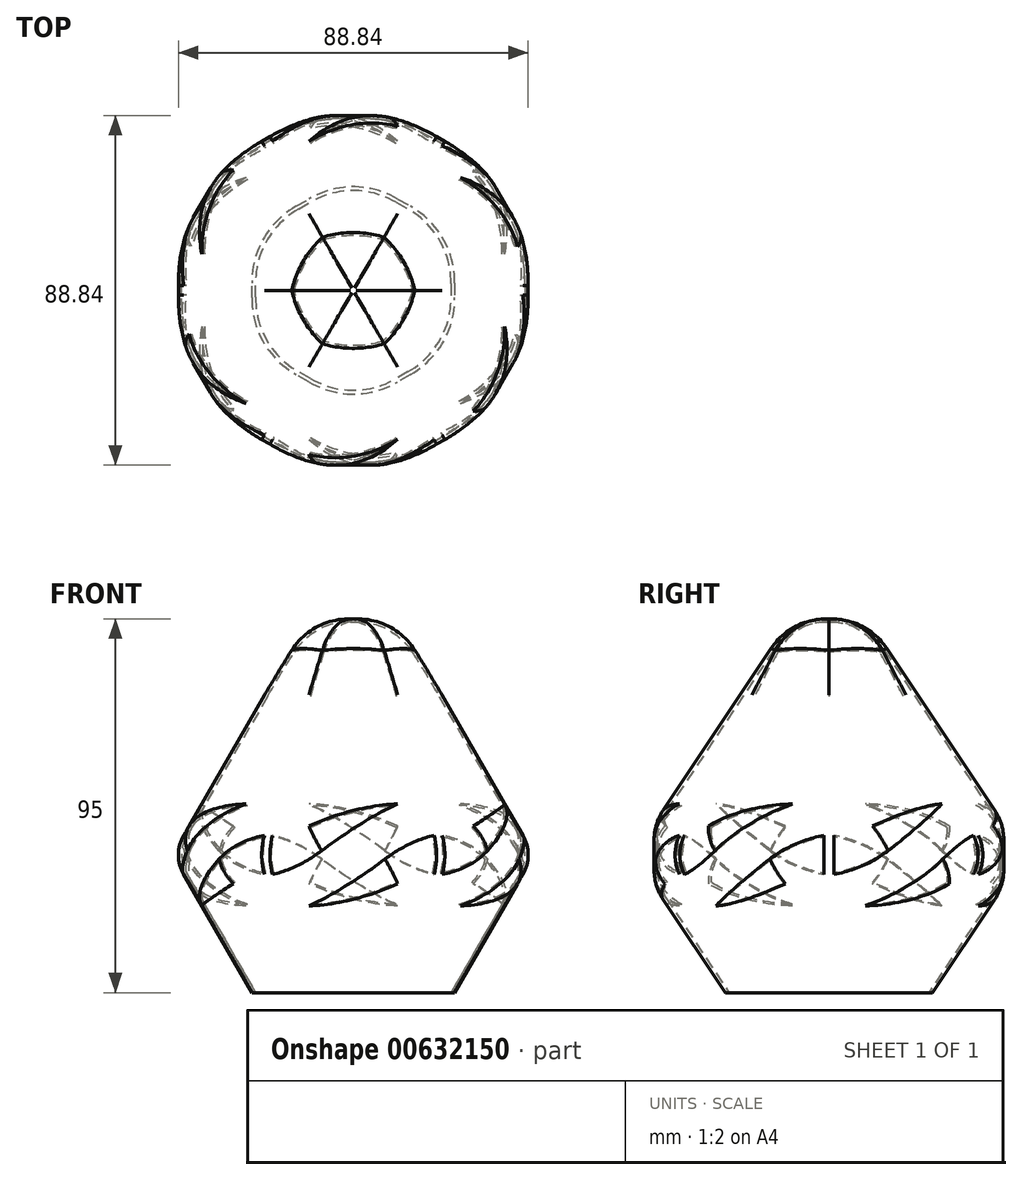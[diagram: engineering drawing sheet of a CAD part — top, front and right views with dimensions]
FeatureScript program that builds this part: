
annotation { "Feature Type Name" : "Feature", "Feature Type Description" : "" }
export const myFeature = defineFeature(function(context is Context, id is Id, definition is map)
    precondition{}
    {
        {
            var Q0;
            Q0=qCreatedBy(makeId("Top.planeOp"),FACE);
            var sketch = newSketch(context, id + "F0", { "sketchPlane" : qUnion([Q0])});
            skCircle(sketch, "E0.cCircle", {"center": v(0, 0) * mm, "radius": 29.75 * mm, "construction": true});
            skLineSegment(sketch, "E0.0", {"start": v(0, -29.75) * mm, "end": v(-25.76, -14.87) * mm});
            skLineSegment(sketch, "E0.1", {"start": v(-25.76, -14.88) * mm, "end": v(-25.76, 14.87) * mm});
            skLineSegment(sketch, "E0.2", {"start": v(-25.76, 14.87) * mm, "end": v(0, 29.75) * mm});
            skLineSegment(sketch, "E0.3", {"start": v(0, 29.75) * mm, "end": v(25.76, 14.88) * mm});
            skLineSegment(sketch, "E0.4", {"start": v(25.76, 14.88) * mm, "end": v(25.76, -14.87) * mm});
            skLineSegment(sketch, "E0.5", {"start": v(25.76, -14.87) * mm, "end": v(0, -29.75) * mm});
            skSolve(sketch);
        }
        {
            var Q0;
            Q0=makeQuery(id+"F0.imprint","IMPRINT",FACE,{"disambiguationData":[TD([[makeQuery(id+"F0.imprint","IMPRINT",EDGE,{"derivedFrom":sQuery(id+"F0.wireOp",EDGE,"E0.0")}),-1.0]])]});
            extrude(context, id + "F1", {"entities" : qUnion([Q0]), "depth" : 35 * mm, "offsetDistance" : 25 * mm, "hasDraft" : true, "draftAngle" : 30 * degree});
        }
        {
            var Q0;
            Q0=makeQuery(id+"F1.opExtrude","CAP_FACE",FACE,{"disambiguationData":[OSD([sQuery(id+"F0.wireOp",EDGE,"E0.0"),sQuery(id+"F0.wireOp",EDGE,"E0.1"),sQuery(id+"F0.wireOp",EDGE,"E0.2"),sQuery(id+"F0.wireOp",EDGE,"E0.3"),sQuery(id+"F0.wireOp",EDGE,"E0.4"),sQuery(id+"F0.wireOp",EDGE,"E0.5")])],"isStart":false});
            extrude(context, id + "F2", {"entities" : qUnion([Q0]), "operationType" : NewBodyOperationType.ADD, "depth" : 60 * mm, "offsetDistance" : 25 * mm, "hasDraft" : true, "draftAngle" : 30 * degree, "draftPullDirection" : true});
        }
        {
            var Q0;
            {var subQ0=sQuery(id+"F0.wireOp",EDGE,"E0.0");Q0=makeQuery(id+"F2.boolean.opBoolean","MERGE",EDGE,{"derivedFrom":[makeQuery(id+"F1.opExtrude","CAP_EDGE",EDGE,{"disambiguationData":[OSD([subQ0])],"isStart":false}),makeQuery(id+"F2.opExtrude","CAP_EDGE",EDGE,{"disambiguationData":[OSD([subQ0])],"isStart":true})]});}
            var Q1;
            {var subQ0=sQuery(id+"F0.wireOp",EDGE,"E0.1");Q1=makeQuery(id+"F2.boolean.opBoolean","MERGE",EDGE,{"derivedFrom":[makeQuery(id+"F1.opExtrude","CAP_EDGE",EDGE,{"disambiguationData":[OSD([subQ0])],"isStart":false}),makeQuery(id+"F2.opExtrude","CAP_EDGE",EDGE,{"disambiguationData":[OSD([subQ0])],"isStart":true})]});}
            var Q2;
            {var subQ0=sQuery(id+"F0.wireOp",EDGE,"E0.2");Q2=makeQuery(id+"F2.boolean.opBoolean","MERGE",EDGE,{"derivedFrom":[makeQuery(id+"F1.opExtrude","CAP_EDGE",EDGE,{"disambiguationData":[OSD([subQ0])],"isStart":false}),makeQuery(id+"F2.opExtrude","CAP_EDGE",EDGE,{"disambiguationData":[OSD([subQ0])],"isStart":true})]});}
            var Q3;
            {var subQ0=sQuery(id+"F0.wireOp",EDGE,"E0.3");Q3=makeQuery(id+"F2.boolean.opBoolean","MERGE",EDGE,{"derivedFrom":[makeQuery(id+"F1.opExtrude","CAP_EDGE",EDGE,{"disambiguationData":[OSD([subQ0])],"isStart":false}),makeQuery(id+"F2.opExtrude","CAP_EDGE",EDGE,{"disambiguationData":[OSD([subQ0])],"isStart":true})]});}
            var Q4;
            {var subQ0=sQuery(id+"F0.wireOp",EDGE,"E0.4");Q4=makeQuery(id+"F2.boolean.opBoolean","MERGE",EDGE,{"derivedFrom":[makeQuery(id+"F1.opExtrude","CAP_EDGE",EDGE,{"disambiguationData":[OSD([subQ0])],"isStart":false}),makeQuery(id+"F2.opExtrude","CAP_EDGE",EDGE,{"disambiguationData":[OSD([subQ0])],"isStart":true})]});}
            var Q5;
            {var subQ0=sQuery(id+"F0.wireOp",EDGE,"E0.5");Q5=makeQuery(id+"F2.boolean.opBoolean","MERGE",EDGE,{"derivedFrom":[makeQuery(id+"F1.opExtrude","CAP_EDGE",EDGE,{"disambiguationData":[OSD([subQ0])],"isStart":false}),makeQuery(id+"F2.opExtrude","CAP_EDGE",EDGE,{"disambiguationData":[OSD([subQ0])],"isStart":true})]});}
            fillet(context, id + "F3", {"entities" : qUnion([Q0, Q1, Q2, Q3, Q4, Q5]), "radius" : 10 * mm, "tangentPropagation" : true, "allowEdgeOverflow" : false});
        }
        {
            var Q0;
            Q0=makeQuery(id+"F2.opExtrude","SWEPT_EDGE",EDGE,{"disambiguationData":[OSD([sQuery(id+"F0.wireOp",EDGE,"E0.4"),sQuery(id+"F0.wireOp",EDGE,"E0.5")])]});
            var Q1;
            Q1=makeQuery(id+"F2.opExtrude","SWEPT_EDGE",EDGE,{"disambiguationData":[OSD([sQuery(id+"F0.wireOp",EDGE,"E0.0"),sQuery(id+"F0.wireOp",EDGE,"E0.5")])]});
            var Q2;
            Q2=makeQuery(id+"F2.opExtrude","SWEPT_EDGE",EDGE,{"disambiguationData":[OSD([sQuery(id+"F0.wireOp",EDGE,"E0.0"),sQuery(id+"F0.wireOp",EDGE,"E0.1")])]});
            var Q3;
            Q3=makeQuery(id+"F2.opExtrude","SWEPT_EDGE",EDGE,{"disambiguationData":[OSD([sQuery(id+"F0.wireOp",EDGE,"E0.1"),sQuery(id+"F0.wireOp",EDGE,"E0.2")])]});
            var Q4;
            Q4=makeQuery(id+"F2.opExtrude","SWEPT_EDGE",EDGE,{"disambiguationData":[OSD([sQuery(id+"F0.wireOp",EDGE,"E0.2"),sQuery(id+"F0.wireOp",EDGE,"E0.3")])]});
            var Q5;
            Q5=makeQuery(id+"F2.opExtrude","SWEPT_EDGE",EDGE,{"disambiguationData":[OSD([sQuery(id+"F0.wireOp",EDGE,"E0.3"),sQuery(id+"F0.wireOp",EDGE,"E0.4")])]});
            var Q6;
            Q6=makeQuery(id+"F2.opExtrude","SWEPT_FACE",FACE,{"disambiguationData":[OSD([sQuery(id+"F0.wireOp",EDGE,"E0.3")])]});
            var Q7;
            Q7=makeQuery(id+"F1.opExtrude","SWEPT_EDGE",EDGE,{"disambiguationData":[OSD([sQuery(id+"F0.wireOp",EDGE,"E0.3"),sQuery(id+"F0.wireOp",EDGE,"E0.4")])]});
            var Q8;
            Q8=makeQuery(id+"F1.opExtrude","SWEPT_EDGE",EDGE,{"disambiguationData":[OSD([sQuery(id+"F0.wireOp",EDGE,"E0.2"),sQuery(id+"F0.wireOp",EDGE,"E0.3")])]});
            var Q9;
            Q9=makeQuery(id+"F1.opExtrude","SWEPT_EDGE",EDGE,{"disambiguationData":[OSD([sQuery(id+"F0.wireOp",EDGE,"E0.1"),sQuery(id+"F0.wireOp",EDGE,"E0.2")])]});
            var Q10;
            Q10=makeQuery(id+"F1.opExtrude","SWEPT_EDGE",EDGE,{"disambiguationData":[OSD([sQuery(id+"F0.wireOp",EDGE,"E0.0"),sQuery(id+"F0.wireOp",EDGE,"E0.1")])]});
            var Q11;
            Q11=makeQuery(id+"F1.opExtrude","SWEPT_EDGE",EDGE,{"disambiguationData":[OSD([sQuery(id+"F0.wireOp",EDGE,"E0.0"),sQuery(id+"F0.wireOp",EDGE,"E0.5")])]});
            fillet(context, id + "F4", {"entities" : qUnion([Q0, Q1, Q2, Q3, Q4, Q5, Q6, Q7, Q8, Q9, Q10, Q11]), "radius" : 26 * mm, "tangentPropagation" : true, "allowEdgeOverflow" : false});
        }
        {
            var Q0;
            Q0=makeQuery(id+"F2.opExtrude","CAP_FACE",FACE,{"disambiguationData":[OSD([sQuery(id+"F0.wireOp",EDGE,"E0.0"),sQuery(id+"F0.wireOp",EDGE,"E0.1"),sQuery(id+"F0.wireOp",EDGE,"E0.2"),sQuery(id+"F0.wireOp",EDGE,"E0.3"),sQuery(id+"F0.wireOp",EDGE,"E0.4"),sQuery(id+"F0.wireOp",EDGE,"E0.5")])],"isStart":false});
            fillet(context, id + "F5", {"entities" : qUnion([Q0]), "radius" : 17 * mm, "tangentPropagation" : true, "allowEdgeOverflow" : false});
        }
        {
            var Q0;
            Q0=makeQuery(id+"F1.opExtrude","CAP_FACE",FACE,{"disambiguationData":[OSD([sQuery(id+"F0.wireOp",EDGE,"E0.0"),sQuery(id+"F0.wireOp",EDGE,"E0.1"),sQuery(id+"F0.wireOp",EDGE,"E0.2"),sQuery(id+"F0.wireOp",EDGE,"E0.3"),sQuery(id+"F0.wireOp",EDGE,"E0.4"),sQuery(id+"F0.wireOp",EDGE,"E0.5")])],"isStart":true});
            shell(context, id + "F6", {"entities" : qUnion([Q0]), "thickness" : 0.8 * mm});
        }
    });
